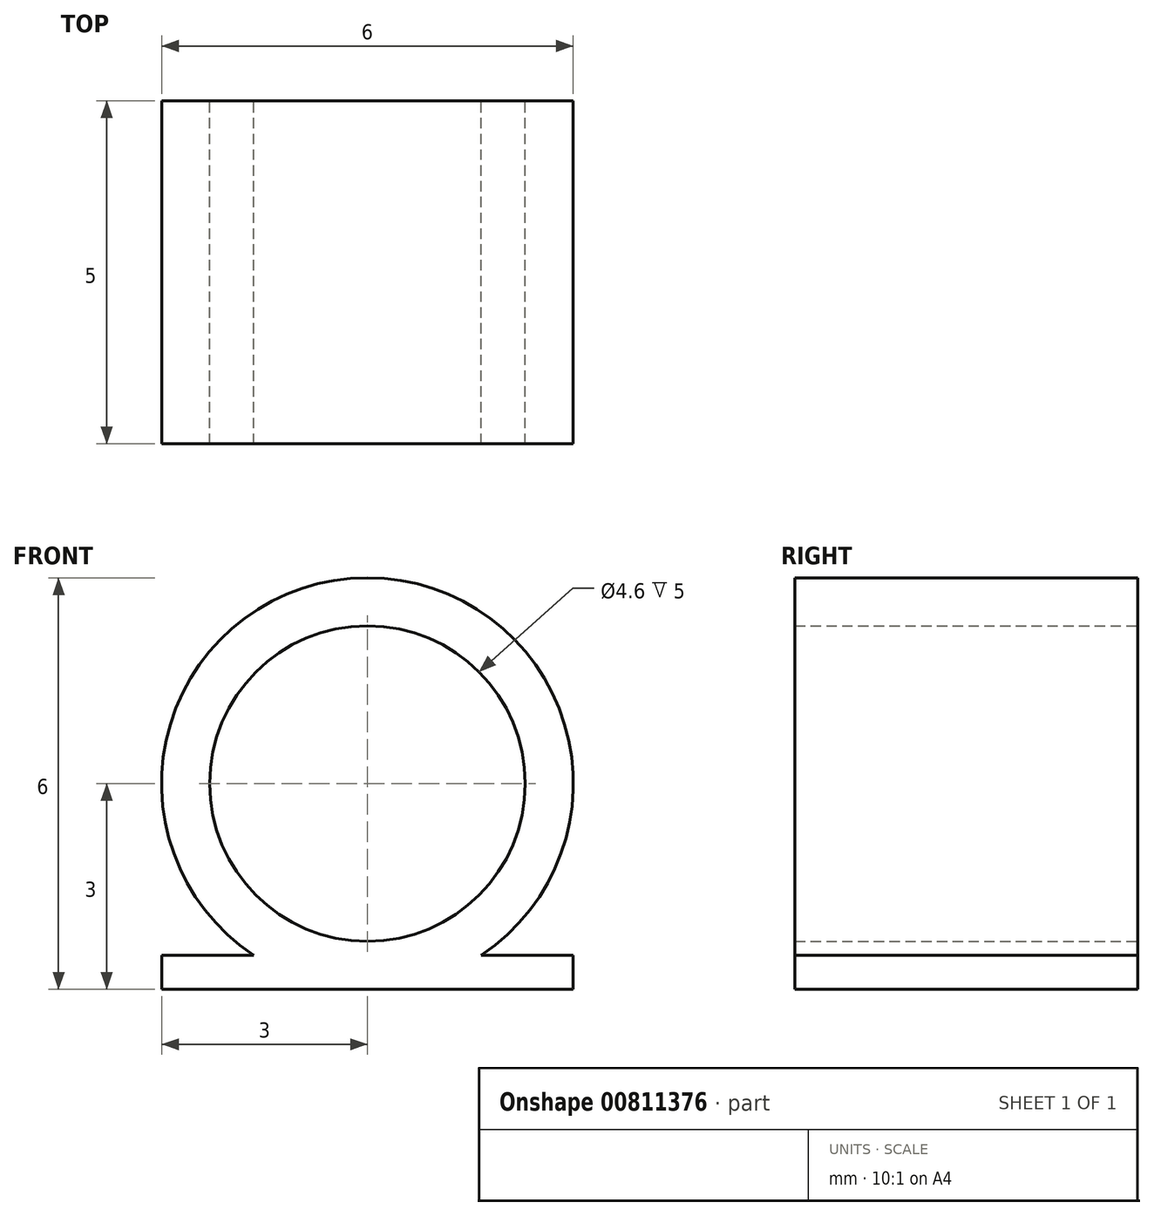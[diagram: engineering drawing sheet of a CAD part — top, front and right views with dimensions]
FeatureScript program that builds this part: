
annotation { "Feature Type Name" : "Feature", "Feature Type Description" : "" }
export const myFeature = defineFeature(function(context is Context, id is Id, definition is map)
    precondition{}
    {
        {
            var Q0;
            Q0=qCreatedBy(makeId("Front.planeOp"),FACE);
            var sketch = newSketch(context, id + "F0", { "sketchPlane" : qUnion([Q0])});
            skCircle(sketch, "E0", {"center": v(0, 0) * mm, "radius": 2.3 * mm});
            skCircle(sketch, "E1", {"center": v(0, 0) * mm, "radius": 3 * mm});
            skSolve(sketch);
        }
        {
            var Q0;
            Q0=makeQuery(id+"F0.imprint","IMPRINT",FACE,{"disambiguationData":[TD([[makeQuery(id+"F0.imprint","IMPRINT",EDGE,{"derivedFrom":sQuery(id+"F0.wireOp",EDGE,"E0")}),-1.0]])]});
            extrude(context, id + "F1", {"entities" : qUnion([Q0]), "depth" : 5 * mm, "offsetDistance" : 25 * mm});
        }
        {
            var Q0;
            Q0=qCreatedBy(makeId("Top.planeOp"),FACE);
            var sketch = newSketch(context, id + "F2", { "sketchPlane" : qUnion([Q0])});
            skLineSegment(sketch, "E2", {"start": v(3, 0) * mm, "end": v(3, -5) * mm});
            skLineSegment(sketch, "E3", {"start": v(-3, -5) * mm, "end": v(-3, 0) * mm});
            skLineSegment(sketch, "E4.0", {"start": v(3, 0) * mm, "end": v(-3, 0) * mm});
            skLineSegment(sketch, "E5.0", {"start": v(3, -5) * mm, "end": v(-3, -5) * mm});
            skSolve(sketch);
        }
        {
            var Q0;
            Q0 = qSketchRegion(id + "F2", true);
            extrude(context, id + "F3", {"entities" : qUnion([Q0]), "operationType" : NewBodyOperationType.ADD, "oppositeDirection" : true, "depth" : 3 * mm, "offsetDistance" : 25 * mm, "hasSecondDirection" : true, "secondDirectionOppositeDirection" : true, "secondDirectionDepth" : 2.5 * mm});
        }
    });
